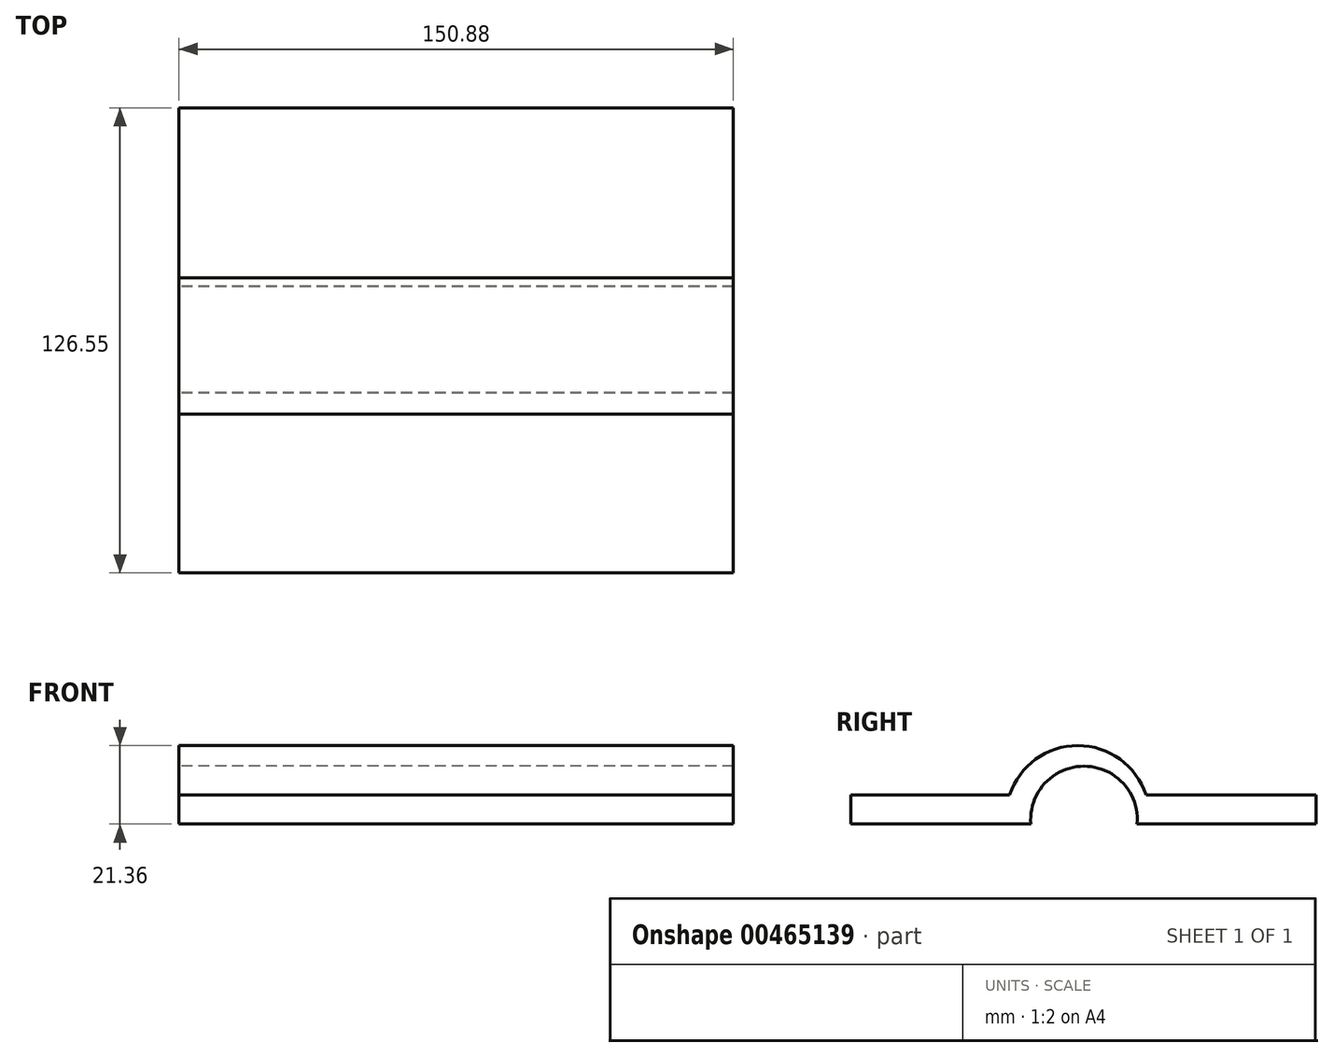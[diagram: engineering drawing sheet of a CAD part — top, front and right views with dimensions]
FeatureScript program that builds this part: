
annotation { "Feature Type Name" : "Feature", "Feature Type Description" : "" }
export const myFeature = defineFeature(function(context is Context, id is Id, definition is map)
    precondition{}
    {
        {
            var Q0;
            Q0=qCreatedBy(makeId("Right.planeOp"),FACE);
            var sketch = newSketch(context, id + "F0", { "sketchPlane" : qUnion([Q0])});
            skLineSegment(sketch, "E0", {"start": v(-68, 10.95) * mm, "end": v(-19.01, 10.95) * mm});
            skArc(sketch, "E1", {"start": v(9.89, 10.95) * mm, "mid": v(-4.56, 26.7) * mm, "end": v(-19.01, 10.95) * mm});
            skLineSegment(sketch, "E2", {"start": v(9.89, 10.95) * mm, "end": v(58.56, 10.95) * mm});
            skLineSegment(sketch, "E3", {"start": v(-68, 10.95) * mm, "end": v(-68, 18.86) * mm});
            skLineSegment(sketch, "E4", {"start": v(-68, 18.86) * mm, "end": v(-24.8, 18.86) * mm});
            skLineSegment(sketch, "E5", {"start": v(12.32, 18.86) * mm, "end": v(58.56, 18.86) * mm});
            skLineSegment(sketch, "E6", {"start": v(58.56, 18.86) * mm, "end": v(58.56, 10.95) * mm});
            skArc(sketch, "E7", {"start": v(12.32, 18.86) * mm, "mid": v(-6.24, 32.31) * mm, "end": v(-24.8, 18.86) * mm});
            skSolve(sketch);
        }
        {
            var Q0;
            Q0=makeQuery(id+"F0.imprint","IMPRINT",FACE,{"disambiguationData":[TD([[makeQuery(id+"F0.imprint","IMPRINT",EDGE,{"derivedFrom":sQuery(id+"F0.wireOp",EDGE,"E0")}),1.0]])]});
            extrude(context, id + "F1", {"entities" : qUnion([Q0]), "depth" : 150.88 * mm, "symmetric" : true});
        }
    });
